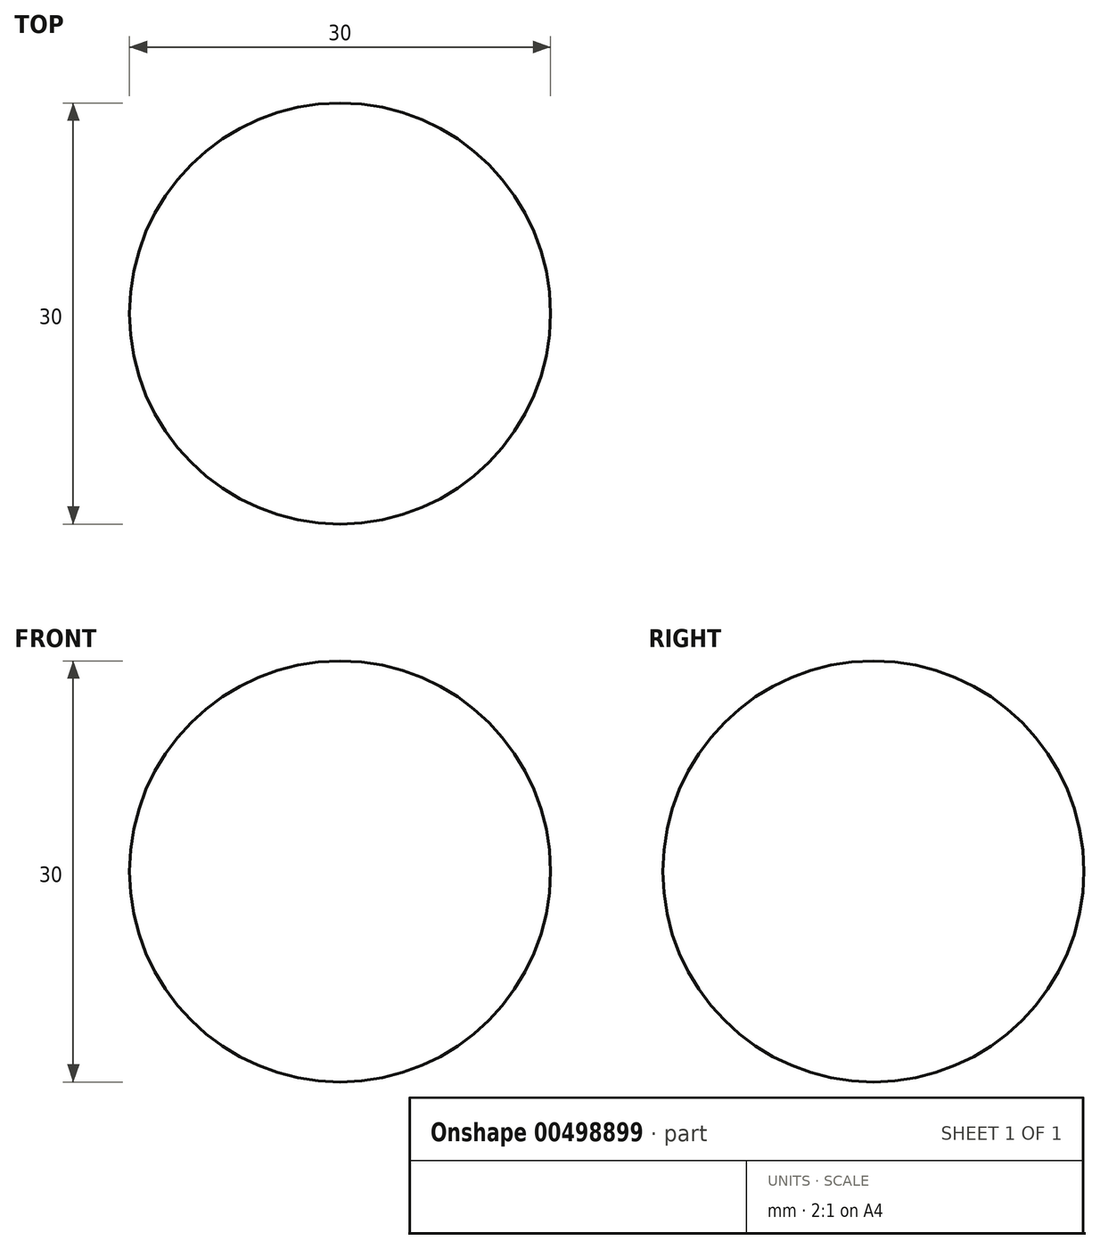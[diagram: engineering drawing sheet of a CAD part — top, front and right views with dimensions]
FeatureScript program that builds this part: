
annotation { "Feature Type Name" : "Feature", "Feature Type Description" : "" }
export const myFeature = defineFeature(function(context is Context, id is Id, definition is map)
    precondition{}
    {
        {
            var Q0;
            Q0=qCreatedBy(makeId("Front.planeOp"),FACE);
            var sketch = newSketch(context, id + "F0", { "sketchPlane" : qUnion([Q0])});
            skArc(sketch, "E0", {"start": v(0, -15) * mm, "mid": v(15, 0) * mm, "end": v(0, 15) * mm});
            skLineSegment(sketch, "E1", {"start": v(0, 15) * mm, "end": v(0, -15) * mm});
            skSolve(sketch);
        }
        {
            var Q0;
            Q0=makeQuery(id+"F0.imprint","IMPRINT",FACE,{"disambiguationData":[TD([[makeQuery(id+"F0.imprint","IMPRINT",EDGE,{"derivedFrom":sQuery(id+"F0.wireOp",EDGE,"E0")}),1.0]])]});
            var Q1;
            Q1=sQuery(id+"F0.wireOp",EDGE,"E1");
            revolve(context, id + "F1", {"entities" : qUnion([Q0]), "axis" : qUnion([Q1]), "revolveType" : RevolveType.FULL});
        }
    });
